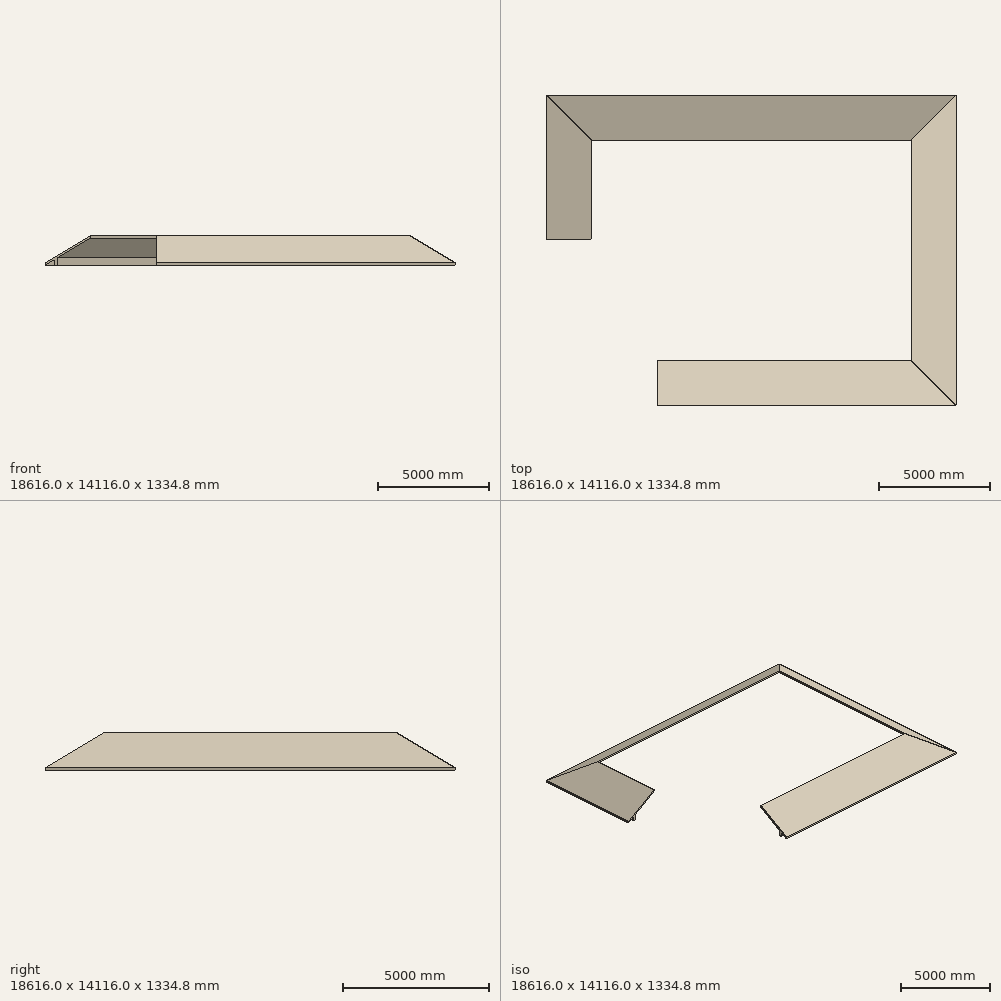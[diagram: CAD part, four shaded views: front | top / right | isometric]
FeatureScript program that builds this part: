
annotation { "Feature Type Name" : "Feature", "Feature Type Description" : "" }
export const myFeature = defineFeature(function(context is Context, id is Id, definition is map)
    precondition{}
    {
        {
            var Q0;
            Q0=qCreatedBy(makeId("Front.planeOp"),FACE);
            var sketch = newSketch(context, id + "F0", { "sketchPlane" : qUnion([Q0])});
            skLineSegment(sketch, "E0", {"start": v(0, 900) * mm, "end": v(-1500, 0) * mm});
            skLineSegment(sketch, "E1", {"start": v(-1500, 0) * mm, "end": v(-1500, 0) * mm});
            skLineSegment(sketch, "E2", {"start": v(-2057.98, -334.79) * mm, "end": v(-2057.98, -234.79) * mm});
            skLineSegment(sketch, "E3", {"start": v(-2057.98, -234.79) * mm, "end": v(0, 1000) * mm});
            skLineSegment(sketch, "E4", {"start": v(0, 1000) * mm, "end": v(0, 900) * mm});
            skLineSegment(sketch, "E5.bottom", {"start": v(-1500, -334.79) * mm, "end": v(-1650, -334.79) * mm});
            skLineSegment(sketch, "E5.left", {"start": v(-1500, -334.79) * mm, "end": v(-1500, 0) * mm});
            skLineSegment(sketch, "E5.right", {"start": v(-1650, -334.79) * mm, "end": v(-1650, -90) * mm});
            skLineSegment(sketch, "E6.trimOffspring", {"start": v(-1650, -90) * mm, "end": v(-2057.98, -334.79) * mm});
            skSolve(sketch);
        }
        {
            var Q0;
            Q0 = qSketchRegion(id + "F0", true);
            extrude(context, id + "F1", {"entities" : qUnion([Q0]), "oppositeDirection" : true, "depth" : 6558 * mm, "offsetDistance" : 25 * mm});
        }
        {
            var Q0;
            Q0=makeQuery(id+"F1.opExtrude","SWEPT_FACE",FACE,{"disambiguationData":[OSD([sQuery(id+"F0.wireOp",EDGE,"E2")])]});
            var sketch = newSketch(context, id + "F2", { "sketchPlane" : qUnion([Q0])});
            skLineSegment(sketch, "E7", {"start": v(-4500.02, 900) * mm, "end": v(-6000.02, 0) * mm});
            skLineSegment(sketch, "E8", {"start": v(-6000.02, 0) * mm, "end": v(-6000.02, 0) * mm});
            skLineSegment(sketch, "E9", {"start": v(-6558, -334.79) * mm, "end": v(-6558, -234.79) * mm});
            skLineSegment(sketch, "E10", {"start": v(-6558, -234.79) * mm, "end": v(-4500.02, 1000) * mm});
            skLineSegment(sketch, "E11", {"start": v(-4500.02, 1000) * mm, "end": v(-4500.02, 900) * mm});
            skLineSegment(sketch, "E12.bottom", {"start": v(-6000.02, -334.79) * mm, "end": v(-6150.02, -334.79) * mm});
            skLineSegment(sketch, "E12.left", {"start": v(-6000.02, -334.79) * mm, "end": v(-6000.02, 0) * mm});
            skLineSegment(sketch, "E12.right", {"start": v(-6150.02, -334.79) * mm, "end": v(-6150.02, -90) * mm});
            skLineSegment(sketch, "E13.trimOffspring", {"start": v(-6150.02, -90) * mm, "end": v(-6558, -334.79) * mm});
            skSolve(sketch);
        }
        {
            var Q0;
            Q0 = qSketchRegion(id + "F2", true);
            extrude(context, id + "F3", {"entities" : qUnion([Q0]), "operationType" : NewBodyOperationType.ADD, "oppositeDirection" : true, "depth" : 18616 * mm, "offsetDistance" : 25 * mm});
        }
        {
            var Q0;
            {var subQ2=sQuery(id+"F2.wireOp",EDGE,"E11");var subQ3=makeQuery(id+"F3.opExtrude","SWEPT_FACE",FACE,{"disambiguationData":[OSD([subQ2])]});Q0=makeQuery(id+"F3.boolean.opBoolean","SPLIT",FACE,{"disambiguationData":[TD([makeQuery(id+"F1.opExtrude","SWEPT_FACE",FACE,{"disambiguationData":[OSD([sQuery(id+"F0.wireOp",EDGE,"E2")])]})])],"derivedFrom":subQ3});}
            var sketch = newSketch(context, id + "F4", { "sketchPlane" : qUnion([Q0])});
            skLineSegment(sketch, "E14", {"start": v(-2057.98, 1000) * mm, "end": v(0, 1000) * mm});
            skLineSegment(sketch, "E15", {"start": v(0, 1000) * mm, "end": v(-2057.98, -234.79) * mm});
            skLineSegment(sketch, "E16", {"start": v(-2057.98, -234.79) * mm, "end": v(-2057.98, 1000) * mm});
            skSolve(sketch);
        }
        {
            var Q0;
            Q0 = qSketchRegion(id + "F4", true);
            extrude(context, id + "F5", {"entities" : qUnion([Q0]), "operationType" : NewBodyOperationType.REMOVE, "endBound" : BoundingType.THROUGH_ALL, "oppositeDirection" : true, "depth" : 25 * mm, "offsetDistance" : 25 * mm});
        }
        {
            var Q0;
            {var subQ1=sQuery(id+"F0.wireOp",EDGE,"E4");var subQ3=makeQuery(id+"F1.opExtrude","SWEPT_FACE",FACE,{"disambiguationData":[OSD([subQ1])]});Q0=makeQuery(id+"F3.boolean.opBoolean","SPLIT",FACE,{"disambiguationData":[TD([makeQuery(id+"F3.opExtrude","SWEPT_FACE",FACE,{"disambiguationData":[OSD([sQuery(id+"F2.wireOp",EDGE,"E9")])]})])],"derivedFrom":subQ3});}
            var sketch = newSketch(context, id + "F6", { "sketchPlane" : qUnion([Q0])});
            skLineSegment(sketch, "E17", {"start": v(4500.02, 1000) * mm, "end": v(6558, 1000) * mm});
            skLineSegment(sketch, "E18", {"start": v(6558, 1000) * mm, "end": v(6558, -234.79) * mm});
            skLineSegment(sketch, "E19", {"start": v(6558, -234.79) * mm, "end": v(4500.02, 1000) * mm});
            skSolve(sketch);
        }
        {
            var Q0;
            Q0 = qSketchRegion(id + "F6", true);
            extrude(context, id + "F7", {"entities" : qUnion([Q0]), "operationType" : NewBodyOperationType.REMOVE, "endBound" : BoundingType.THROUGH_ALL, "oppositeDirection" : true, "depth" : 25 * mm, "offsetDistance" : 25 * mm});
        }
        {
            var Q0;
            Q0=makeQuery(id+"F3.boolean.opBoolean","MERGE",FACE,{"derivedFrom":[makeQuery(id+"F1.opExtrude","CAP_FACE",FACE,{"disambiguationData":[OSD([sQuery(id+"F0.wireOp",EDGE,"E0"),sQuery(id+"F0.wireOp",EDGE,"E2"),sQuery(id+"F0.wireOp",EDGE,"E3"),sQuery(id+"F0.wireOp",EDGE,"E4"),sQuery(id+"F0.wireOp",EDGE,"E5.bottom"),sQuery(id+"F0.wireOp",EDGE,"E5.left"),sQuery(id+"F0.wireOp",EDGE,"E5.right"),sQuery(id+"F0.wireOp",EDGE,"E6.trimOffspring")])],"isStart":false}),makeQuery(id+"F3.opExtrude","SWEPT_FACE",FACE,{"disambiguationData":[OSD([sQuery(id+"F2.wireOp",EDGE,"E9")])]})]});
            var sketch = newSketch(context, id + "F8", { "sketchPlane" : qUnion([Q0])});
            skLineSegment(sketch, "E20", {"start": v(-14500.03, 900) * mm, "end": v(-16000.03, 0) * mm});
            skLineSegment(sketch, "E21", {"start": v(-16000.03, 0) * mm, "end": v(-16000.03, 0) * mm});
            skLineSegment(sketch, "E22", {"start": v(-16558.02, -334.79) * mm, "end": v(-16558.02, -234.79) * mm});
            skLineSegment(sketch, "E23", {"start": v(-16558.02, -234.79) * mm, "end": v(-14500.03, 1000) * mm});
            skLineSegment(sketch, "E24", {"start": v(-14500.03, 1000) * mm, "end": v(-14500.03, 900) * mm});
            skLineSegment(sketch, "E25.bottom", {"start": v(-16000.03, -334.79) * mm, "end": v(-16150.03, -334.79) * mm});
            skLineSegment(sketch, "E25.left", {"start": v(-16000.03, -334.79) * mm, "end": v(-16000.03, 0) * mm});
            skLineSegment(sketch, "E25.right", {"start": v(-16150.03, -334.79) * mm, "end": v(-16150.03, -90) * mm});
            skLineSegment(sketch, "E26.trimOffspring", {"start": v(-16150.03, -90) * mm, "end": v(-16558.02, -334.79) * mm});
            skSolve(sketch);
        }
        {
            var Q0;
            Q0 = qSketchRegion(id + "F8", true);
            extrude(context, id + "F9", {"entities" : qUnion([Q0]), "operationType" : NewBodyOperationType.ADD, "oppositeDirection" : true, "depth" : 14116 * mm, "offsetDistance" : 25 * mm});
        }
        {
            var Q0;
            {var subQ0=sQuery(id+"F8.wireOp",EDGE,"E24");var subQ3=makeQuery(id+"F9.opExtrude","SWEPT_FACE",FACE,{"disambiguationData":[OSD([subQ0])]});Q0=makeQuery(id+"F9.boolean.opBoolean","SPLIT",FACE,{"disambiguationData":[TD([makeQuery(id+"F3.opExtrude","SWEPT_FACE",FACE,{"disambiguationData":[OSD([sQuery(id+"F2.wireOp",EDGE,"E9")])]})])],"derivedFrom":subQ3});}
            var sketch = newSketch(context, id + "F10", { "sketchPlane" : qUnion([Q0])});
            skLineSegment(sketch, "E27", {"start": v(-6558, 1000) * mm, "end": v(-4500.02, 1000) * mm});
            skLineSegment(sketch, "E28", {"start": v(-4500.02, 1000) * mm, "end": v(-6558, -234.79) * mm});
            skLineSegment(sketch, "E29", {"start": v(-6558, -234.79) * mm, "end": v(-6558, 1000) * mm});
            skSolve(sketch);
        }
        {
            var Q0;
            Q0 = qSketchRegion(id + "F10", true);
            extrude(context, id + "F11", {"entities" : qUnion([Q0]), "operationType" : NewBodyOperationType.REMOVE, "endBound" : BoundingType.THROUGH_ALL, "oppositeDirection" : true, "depth" : 25 * mm, "offsetDistance" : 25 * mm});
        }
        {
            var Q0;
            {var subQ2=sQuery(id+"F2.wireOp",EDGE,"E11");var subQ5=makeQuery(id+"F3.opExtrude","SWEPT_FACE",FACE,{"disambiguationData":[OSD([subQ2])]});Q0=makeQuery(id+"F9.boolean.opBoolean","SPLIT",FACE,{"disambiguationData":[TD([makeQuery(id+"F9.opExtrude","SWEPT_FACE",FACE,{"disambiguationData":[OSD([sQuery(id+"F8.wireOp",EDGE,"E22")])]})])],"derivedFrom":makeQuery(id+"F3.boolean.opBoolean","SPLIT",FACE,{"disambiguationData":[TD([makeQuery(id+"F1.opExtrude","SWEPT_FACE",FACE,{"disambiguationData":[OSD([sQuery(id+"F0.wireOp",EDGE,"E0")])]})])],"derivedFrom":subQ5})});}
            var sketch = newSketch(context, id + "F12", { "sketchPlane" : qUnion([Q0])});
            skLineSegment(sketch, "E30", {"start": v(16558.02, 1000) * mm, "end": v(16558.02, -234.79) * mm});
            skLineSegment(sketch, "E31", {"start": v(16558.02, -234.79) * mm, "end": v(14500.03, 1000) * mm});
            skLineSegment(sketch, "E32", {"start": v(14500.03, 1000) * mm, "end": v(16558.02, 1000) * mm});
            skSolve(sketch);
        }
        {
            var Q0;
            Q0 = qSketchRegion(id + "F12", true);
            extrude(context, id + "F13", {"entities" : qUnion([Q0]), "operationType" : NewBodyOperationType.REMOVE, "endBound" : BoundingType.THROUGH_ALL, "oppositeDirection" : true, "depth" : 25 * mm, "offsetDistance" : 25 * mm});
        }
        {
            var Q0;
            Q0=makeQuery(id+"F9.boolean.opBoolean","MERGE",FACE,{"derivedFrom":[makeQuery(id+"F3.opExtrude","CAP_FACE",FACE,{"disambiguationData":[OSD([sQuery(id+"F2.wireOp",EDGE,"E7"),sQuery(id+"F2.wireOp",EDGE,"E9"),sQuery(id+"F2.wireOp",EDGE,"E10"),sQuery(id+"F2.wireOp",EDGE,"E11"),sQuery(id+"F2.wireOp",EDGE,"E12.bottom"),sQuery(id+"F2.wireOp",EDGE,"E12.left"),sQuery(id+"F2.wireOp",EDGE,"E12.right"),sQuery(id+"F2.wireOp",EDGE,"E13.trimOffspring")])],"isStart":false}),makeQuery(id+"F9.opExtrude","SWEPT_FACE",FACE,{"disambiguationData":[OSD([sQuery(id+"F8.wireOp",EDGE,"E22")])]})]});
            var sketch = newSketch(context, id + "F14", { "sketchPlane" : qUnion([Q0])});
            skLineSegment(sketch, "E33", {"start": v(-5500.02, 900) * mm, "end": v(-7000.02, 0) * mm});
            skLineSegment(sketch, "E34", {"start": v(-7000.02, 0) * mm, "end": v(-7000.02, 0) * mm});
            skLineSegment(sketch, "E35", {"start": v(-7558, -334.79) * mm, "end": v(-7558, -234.79) * mm});
            skLineSegment(sketch, "E36", {"start": v(-7558, -234.79) * mm, "end": v(-5500.02, 1000) * mm});
            skLineSegment(sketch, "E37", {"start": v(-5500.02, 1000) * mm, "end": v(-5500.02, 900) * mm});
            skLineSegment(sketch, "E38.bottom", {"start": v(-7000.02, -334.79) * mm, "end": v(-7150.02, -334.79) * mm});
            skLineSegment(sketch, "E38.left", {"start": v(-7000.02, -334.79) * mm, "end": v(-7000.02, 0) * mm});
            skLineSegment(sketch, "E38.right", {"start": v(-7150.02, -334.79) * mm, "end": v(-7150.02, -90) * mm});
            skLineSegment(sketch, "E39.trimOffspring", {"start": v(-7150.02, -90) * mm, "end": v(-7558, -334.79) * mm});
            skSolve(sketch);
        }
        {
            var Q0;
            Q0 = qSketchRegion(id + "F14", true);
            extrude(context, id + "F15", {"entities" : qUnion([Q0]), "operationType" : NewBodyOperationType.ADD, "oppositeDirection" : true, "depth" : 13558 * mm, "offsetDistance" : 25 * mm});
        }
        {
            var Q0;
            {var subQ1=sQuery(id+"F14.wireOp",EDGE,"E37");var subQ3=makeQuery(id+"F15.opExtrude","SWEPT_FACE",FACE,{"disambiguationData":[OSD([subQ1])]});Q0=makeQuery(id+"F15.boolean.opBoolean","SPLIT",FACE,{"disambiguationData":[TD([makeQuery(id+"F9.opExtrude","SWEPT_FACE",FACE,{"disambiguationData":[OSD([sQuery(id+"F8.wireOp",EDGE,"E22")])]})])],"derivedFrom":subQ3});}
            var sketch = newSketch(context, id + "F16", { "sketchPlane" : qUnion([Q0])});
            skLineSegment(sketch, "E40", {"start": v(-16558.02, 1000) * mm, "end": v(-14500.03, 1000) * mm});
            skLineSegment(sketch, "E41", {"start": v(-14500.03, 1000) * mm, "end": v(-16558.02, -234.79) * mm});
            skLineSegment(sketch, "E42", {"start": v(-16558.02, -234.79) * mm, "end": v(-16558.02, 1000) * mm});
            skSolve(sketch);
        }
        {
            var Q0;
            Q0 = qSketchRegion(id + "F16", true);
            extrude(context, id + "F17", {"entities" : qUnion([Q0]), "operationType" : NewBodyOperationType.REMOVE, "endBound" : BoundingType.THROUGH_ALL, "oppositeDirection" : true, "depth" : 25 * mm, "offsetDistance" : 25 * mm});
        }
        {
            var Q0;
            {var subQ2=sQuery(id+"F8.wireOp",EDGE,"E24");var subQ5=makeQuery(id+"F9.opExtrude","SWEPT_FACE",FACE,{"disambiguationData":[OSD([subQ2])]});Q0=makeQuery(id+"F15.boolean.opBoolean","SPLIT",FACE,{"disambiguationData":[TD([makeQuery(id+"F15.opExtrude","SWEPT_FACE",FACE,{"disambiguationData":[OSD([sQuery(id+"F14.wireOp",EDGE,"E35")])]})])],"derivedFrom":makeQuery(id+"F9.boolean.opBoolean","SPLIT",FACE,{"disambiguationData":[TD([makeQuery(id+"F3.opExtrude","SWEPT_FACE",FACE,{"disambiguationData":[OSD([sQuery(id+"F2.wireOp",EDGE,"E7")])]})])],"derivedFrom":subQ5})});}
            var sketch = newSketch(context, id + "F18", { "sketchPlane" : qUnion([Q0])});
            skLineSegment(sketch, "E43", {"start": v(5500.02, 1000) * mm, "end": v(7558, 1000) * mm});
            skLineSegment(sketch, "E44", {"start": v(7558, 1000) * mm, "end": v(7558, -234.79) * mm});
            skLineSegment(sketch, "E45", {"start": v(7558, -234.79) * mm, "end": v(5500.02, 1000) * mm});
            skSolve(sketch);
        }
        {
            var Q0;
            Q0 = qSketchRegion(id + "F18", true);
            extrude(context, id + "F19", {"entities" : qUnion([Q0]), "operationType" : NewBodyOperationType.REMOVE, "endBound" : BoundingType.THROUGH_ALL, "oppositeDirection" : true, "depth" : 25 * mm, "offsetDistance" : 25 * mm});
        }
    });
